# Revit family: Diverter-GROHE-Grandera-19939_Series
name_source: partatom
category: Plumbing Fixtures
revit_build: Autodesk Revit 2014 (Build: 20130308_1515(x64)
units: mm (PartAtom-declared; Revit-internal decimal feet)

## types (2) — shared parameters
ADA Compliant = No
Assembly Code = D2010710
CW Connection = Yes
CWFU = 1.5
Cold Water Connection Diameter = 1/2"
Cold Water Connection Radius = 1/4"
Default Elevation = 40"
Description = GRANDERA Dual Function Thermostatic Trim with Control Module
HW Connection = Yes
HWFU = 1.5
Height = 6 11/16"
Hot Water Connection Diameter = 1"
Hot Water Connection Radius = 1/4"
Installation Type = Wall Mounted
Length = 3 3/8"
Manufacturer = Grohe
Price = Prices may vary. Please consult Manufacturer Representative for most up-to-date price list.
Product Page URL = https://www.grohe.ca
URL = https://www.grohe.com
Vent Connection = No
WFU = 2
Warranty Documentation Link = https://www.grohe.ca
Waste Connection = No
Width = 6 11/16"

## per-type parameters (varying)
| type | Finish | Material |
| 19939000 | Metal-Grohe-000-Chrome | Metal-Grohe-000-Chrome |
| 19939EN0 | Metal-Grohe-EN0-Brushed Nickel | Metal-Grohe-EN0-Brushed Nickel |

note: column(s) folded — value = type name in every type: Model

## geometry (parser evidence)
native form markers: Sweep x5
no freeform markers — native parametric forms only
